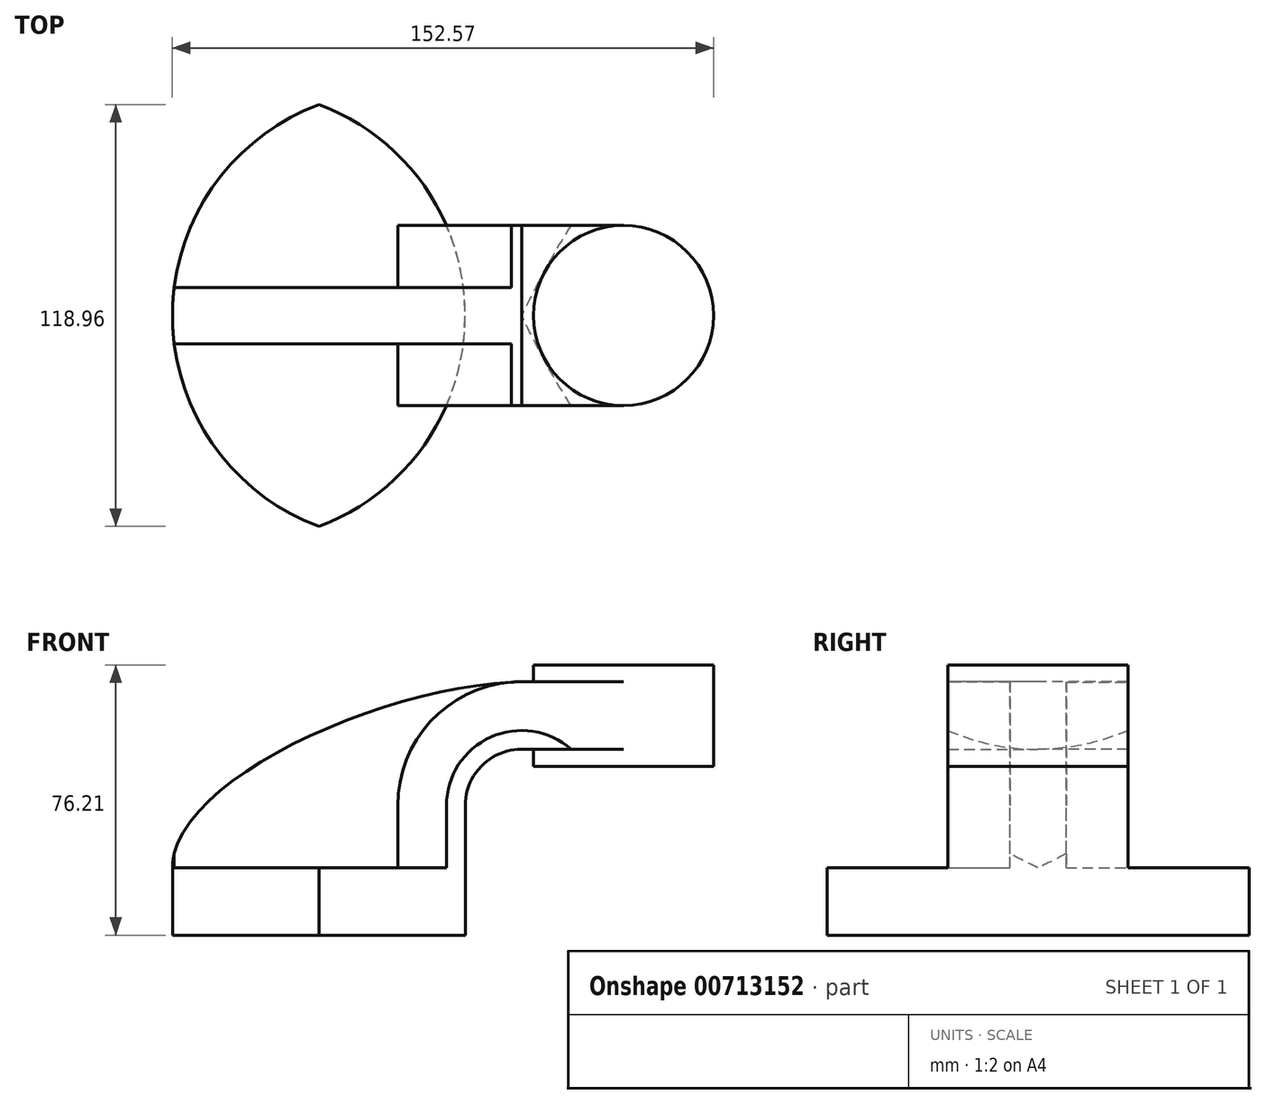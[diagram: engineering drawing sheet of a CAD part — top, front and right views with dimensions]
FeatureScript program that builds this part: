
annotation { "Feature Type Name" : "Feature", "Feature Type Description" : "" }
export const myFeature = defineFeature(function(context is Context, id is Id, definition is map)
    precondition{}
    {
        {
            var Q0;
            Q0=qCreatedBy(makeId("Front.planeOp"),FACE);
            var sketch = newSketch(context, id + "F0", { "sketchPlane" : qUnion([Q0])});
            skLineSegment(sketch, "E0.bottom", {"start": v(41.28, -9.52) * mm, "end": v(-41.28, -9.53) * mm});
            skLineSegment(sketch, "E0.top", {"start": v(41.28, 9.53) * mm, "end": v(-41.28, 9.53) * mm});
            skLineSegment(sketch, "E0.left", {"start": v(41.28, -9.52) * mm, "end": v(41.28, 9.53) * mm});
            skLineSegment(sketch, "E0.right", {"start": v(-41.28, -9.53) * mm, "end": v(-41.28, 9.53) * mm});
            skPoint(sketch, "E0.middle", {"position": v(0, 0) * mm});
            skLineSegment(sketch, "E1.bottom", {"start": v(111.3, 38.1) * mm, "end": v(60.5, 38.1) * mm});
            skLineSegment(sketch, "E1.top", {"start": v(111.3, 66.68) * mm, "end": v(60.5, 66.68) * mm});
            skLineSegment(sketch, "E1.left", {"start": v(111.3, 38.1) * mm, "end": v(111.3, 66.68) * mm});
            skLineSegment(sketch, "E1.right", {"start": v(60.5, 38.1) * mm, "end": v(60.5, 66.68) * mm});
            skPoint(sketch, "E1.middle", {"position": v(85.9, 52.39) * mm});
            skLineSegment(sketch, "E2", {"start": v(41.28, 9.53) * mm, "end": v(41.28, 27) * mm});
            skArc(sketch, "E3", {"start": v(41.27, 27) * mm, "mid": v(45.92, 38.23) * mm, "end": v(57.15, 42.88) * mm});
            skLineSegment(sketch, "E4", {"start": v(57.15, 42.88) * mm, "end": v(85.9, 42.88) * mm});
            skLineSegment(sketch, "E5.0", {"start": v(57.15, 61.93) * mm, "end": v(85.9, 61.93) * mm});
            skArc(sketch, "E5.1", {"start": v(22.23, 27) * mm, "mid": v(32.45, 51.7) * mm, "end": v(57.15, 61.93) * mm});
            skLineSegment(sketch, "E5.2", {"start": v(22.22, 9.53) * mm, "end": v(22.22, 27) * mm});
            skLineSegment(sketch, "E6", {"start": v(85.9, 38.1) * mm, "end": v(85.9, 66.68) * mm});
            skFitSpline(sketch, "E7", {"points": [v(-41.28, 9.52) * mm, v(57.15, 61.93) * mm], "startDerivative": vector(0.52, 74.67) * mm, "endDerivative": vector(116.36, 2.94) * mm});
            skSolve(sketch);
        }
        {
            var Q0;
            Q0=makeQuery(id+"F0.imprint","IMPRINT",FACE,{"disambiguationData":[TD([[makeQuery(id+"F0.imprint","IMPRINT",EDGE,{"derivedFrom":sQuery(id+"F0.wireOp",EDGE,"E0.bottom")}),-1.0]])]});
            extrude(context, id + "F1", {"entities" : qUnion([Q0]), "endBound" : BoundingType.SYMMETRIC, "depth" : 127 * mm, "offsetDistance" : 25.4 * mm});
        }
        {
            var Q0;
            {var subQ1=sQuery(id+"F0.wireOp",EDGE,"E2");Q0=makeQuery(id+"F0.imprint","IMPRINT",FACE,{"disambiguationData":[TD([[makeQuery(id+"F0.imprint","IMPRINT",EDGE,{"derivedFrom":subQ1}),1.0]])]});}
            var Q1;
            {var subQ0=sQuery(id+"F0.wireOp",EDGE,"E4");var subQ1=sQuery(id+"F0.wireOp",EDGE,"E1.right");var subQ2=makeQuery(id+"F0.imprint","INTERSECT",VERTEX,{"derivedFrom":[subQ1,subQ0]});Q1=makeQuery(id+"F0.imprint","IMPRINT",FACE,{"disambiguationData":[TD([[makeQuery(id+"F0.imprint","IMPRINT",EDGE,{"disambiguationData":[TD([[subQ2,-1.0]])],"derivedFrom":subQ1}),-1.0]])]});}
            extrude(context, id + "F2", {"entities" : qUnion([Q0, Q1]), "operationType" : NewBodyOperationType.ADD, "endBound" : BoundingType.SYMMETRIC, "depth" : 50.8 * mm, "offsetDistance" : 25.4 * mm});
        }
        {
            var Q0;
            {var subQ3=sQuery(id+"F0.wireOp",EDGE,"E5.2");Q0=makeQuery(id+"F0.imprint","IMPRINT",FACE,{"disambiguationData":[TD([[makeQuery(id+"F0.imprint","IMPRINT",EDGE,{"derivedFrom":subQ3}),1.0]])]});}
            extrude(context, id + "F3", {"entities" : qUnion([Q0]), "operationType" : NewBodyOperationType.ADD, "endBound" : BoundingType.SYMMETRIC, "depth" : 15.88 * mm, "offsetDistance" : 25.4 * mm});
        }
        {
            var Q0;
            {var subQ0=sQuery(id+"F0.wireOp",EDGE,"E1.left");Q0=makeQuery(id+"F0.imprint","IMPRINT",FACE,{"disambiguationData":[TD([[makeQuery(id+"F0.imprint","IMPRINT",EDGE,{"derivedFrom":subQ0}),1.0]])]});}
            var Q1;
            Q1=sQuery(id+"F0.wireOp",EDGE,"E6");
            revolve(context, id + "F4", {"operationType" : NewBodyOperationType.ADD, "surfaceOperationType" : NewSurfaceOperationType.NEW, "entities" : qUnion([Q0]), "axis" : qUnion([Q1]), "revolveType" : RevolveType.SYMMETRIC, "angle" : 360 * degree});
        }
        {
            var Q0;
            Q0=makeQuery(id+"F1.opExtrude","CAP_EDGE",EDGE,{"disambiguationData":[OSD([sQuery(id+"F0.wireOp",EDGE,"E0.left")])],"isStart":false});
            var Q1;
            Q1=makeQuery(id+"F1.opExtrude","CAP_EDGE",EDGE,{"disambiguationData":[OSD([sQuery(id+"F0.wireOp",EDGE,"E0.right")])],"isStart":false});
            var Q2;
            Q2=makeQuery(id+"F1.opExtrude","CAP_EDGE",EDGE,{"disambiguationData":[OSD([sQuery(id+"F0.wireOp",EDGE,"E0.left")])],"isStart":true});
            var Q3;
            Q3=makeQuery(id+"F1.opExtrude","CAP_EDGE",EDGE,{"disambiguationData":[OSD([sQuery(id+"F0.wireOp",EDGE,"E0.right")])],"isStart":true});
            fillet(context, id + "F5", {"entities" : qUnion([Q0, Q1, Q2, Q3]), "radius" : 63.5 * mm, "tangentPropagation" : true, "allowEdgeOverflow" : false});
        }
    });
